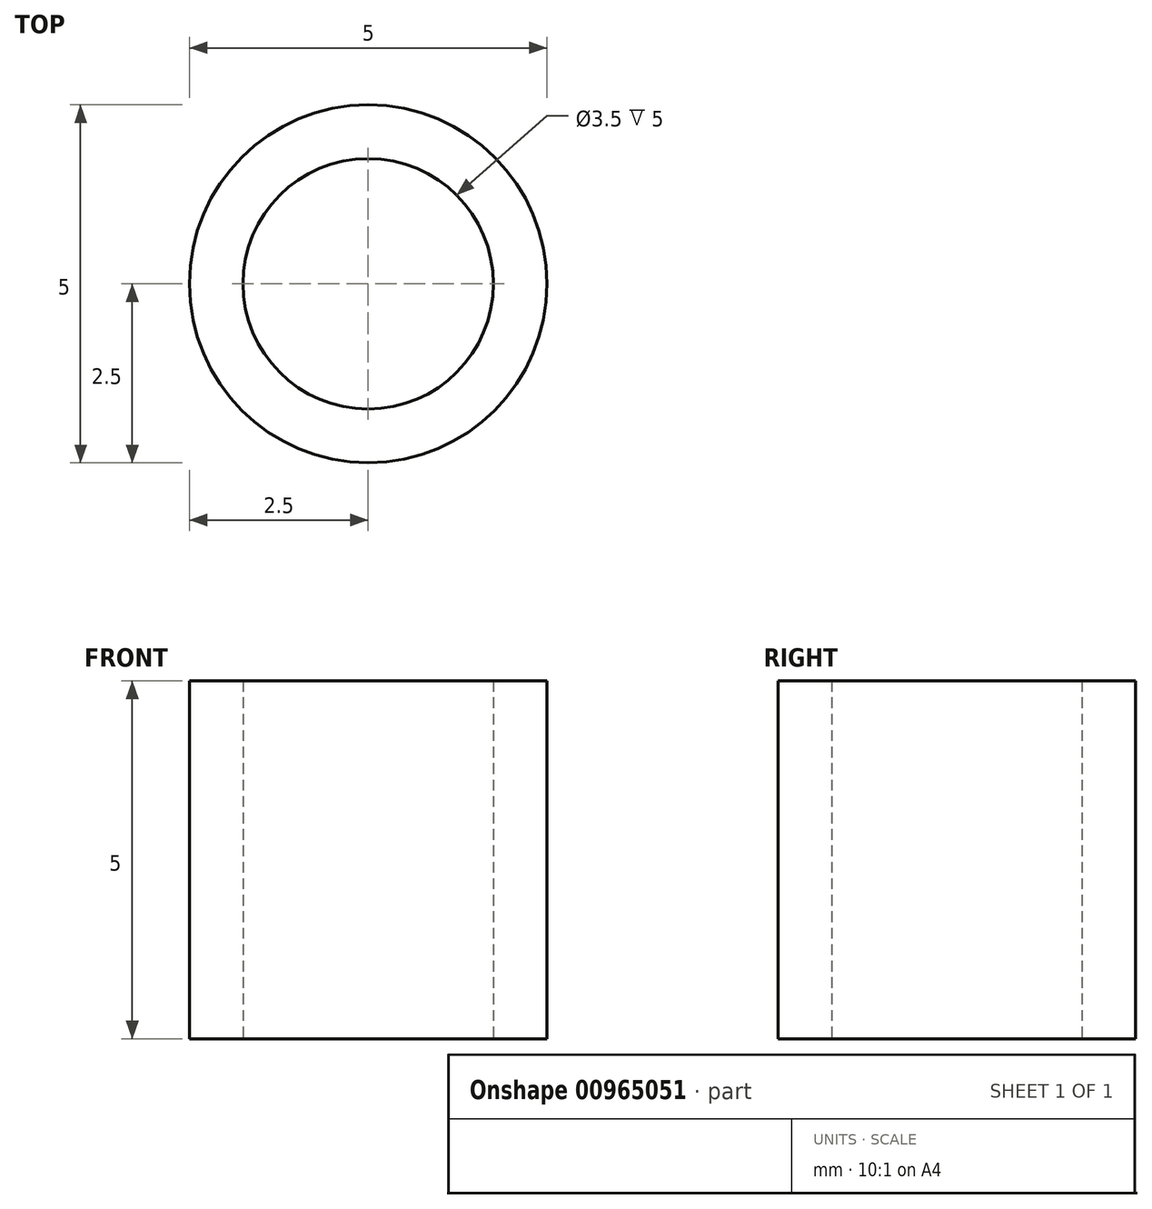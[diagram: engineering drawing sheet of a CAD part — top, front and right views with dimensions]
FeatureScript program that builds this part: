
annotation { "Feature Type Name" : "Feature", "Feature Type Description" : "" }
export const myFeature = defineFeature(function(context is Context, id is Id, definition is map)
    precondition{}
    {
        {
            var Q0;
            Q0=qCreatedBy(makeId("Top.planeOp"),FACE);
            var sketch = newSketch(context, id + "F0", { "sketchPlane" : qUnion([Q0])});
            skCircle(sketch, "E0", {"center": v(0, 0) * mm, "radius": 2.5 * mm});
            skCircle(sketch, "E1", {"center": v(0, 0) * mm, "radius": 1.75 * mm});
            skSolve(sketch);
        }
        {
            var Q0;
            Q0=makeQuery(id+"F0.imprint","IMPRINT",FACE,{"disambiguationData":[TD([[makeQuery(id+"F0.imprint","IMPRINT",EDGE,{"derivedFrom":sQuery(id+"F0.wireOp",EDGE,"E0")}),1.0]])]});
            extrude(context, id + "F1", {"entities" : qUnion([Q0]), "depth" : 5 * mm, "offsetDistance" : 25 * mm});
        }
    });
